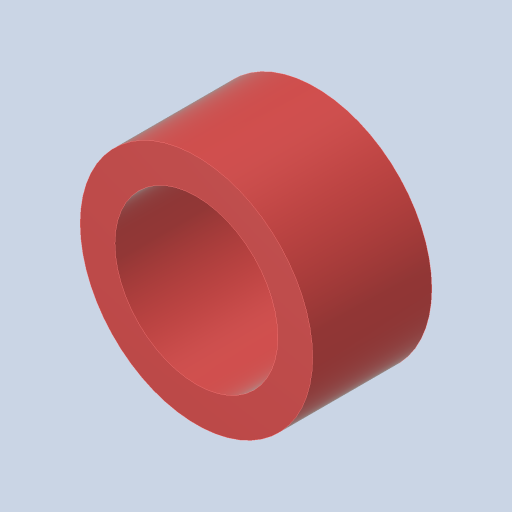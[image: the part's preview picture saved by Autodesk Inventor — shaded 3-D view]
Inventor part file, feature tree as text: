
AUTODESK INVENTOR PART (.ipt)
format: ipt  version: 2023.4 (Build 274418000, 418)  size: 117,760 bytes
history: native  units: in
note: dims shown in document units (in); Inventor stores cm internally (conversion verified against a paired STEP export)
features: extrude x1, sketch x1
ambient origin geometry x8: Origin, YZ Plane, XZ Plane, XY Plane, X Axis, Y Axis, Z Axis, Center Point
bodies: Solid1 (feature_tree)
feature tree (2):
  extrude  "Extrusion1"  Depth=0.428in
  sketch  "Sketch1"  dims[d0=0.585in d1=0.125in d2=0.428in d3=0.0in]
